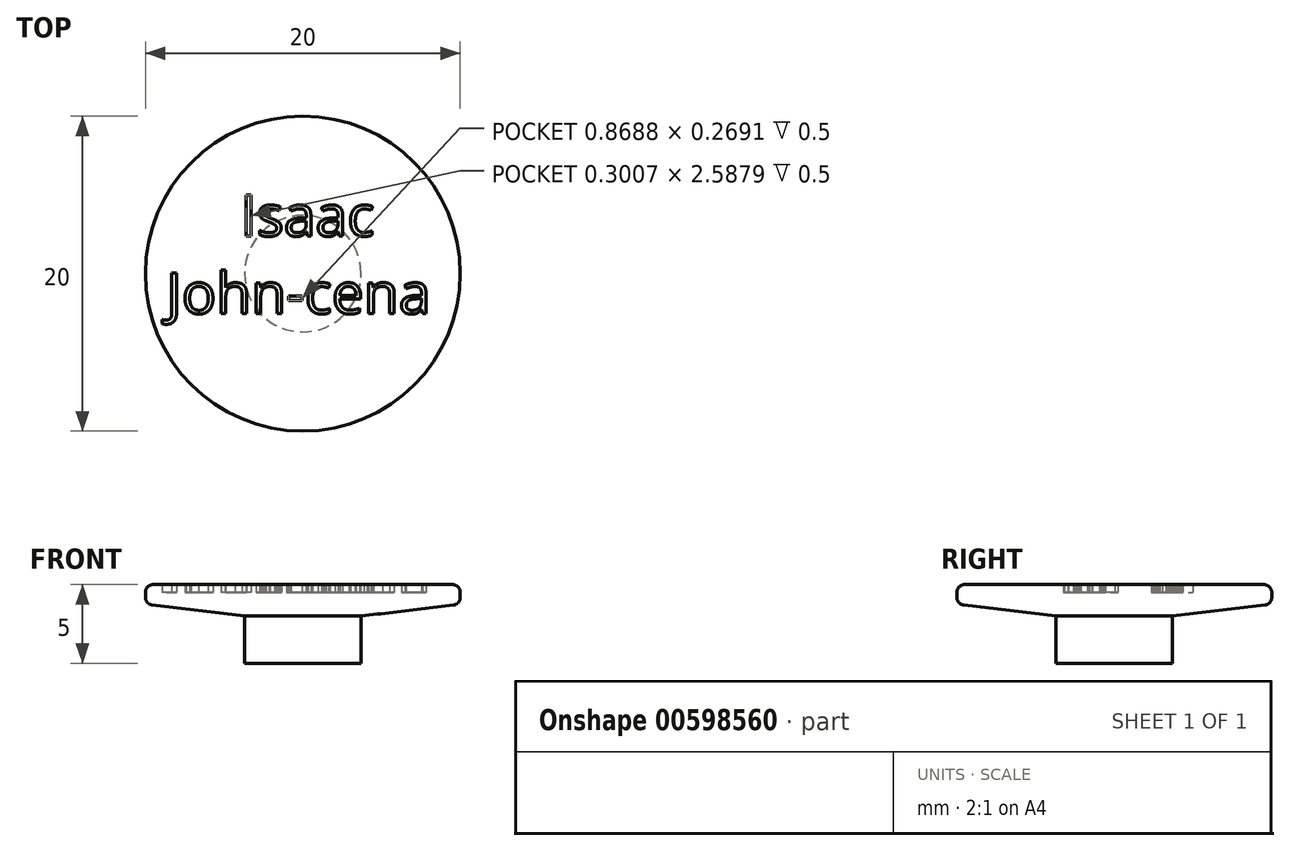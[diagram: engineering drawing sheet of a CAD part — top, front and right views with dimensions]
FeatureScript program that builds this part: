
annotation { "Feature Type Name" : "Feature", "Feature Type Description" : "" }
export const myFeature = defineFeature(function(context is Context, id is Id, definition is map)
    precondition{}
    {
        {
            var Q0;
            Q0=qCreatedBy(makeId("Front.planeOp"),FACE);
            var sketch = newSketch(context, id + "F0", { "sketchPlane" : qUnion([Q0])});
            skLineSegment(sketch, "E0.bottom", {"start": v(0, 0) * mm, "end": v(10, 0) * mm});
            skLineSegment(sketch, "E0.top", {"start": v(0, -1.5) * mm, "end": v(3.7, -1.5) * mm});
            skLineSegment(sketch, "E0.left", {"start": v(0, 0) * mm, "end": v(0, -1.5) * mm});
            skLineSegment(sketch, "E0.right", {"start": v(10, 0) * mm, "end": v(10, -0.75) * mm});
            skLineSegment(sketch, "E1.top", {"start": v(0, -4.5) * mm, "end": v(3.7, -4.5) * mm});
            skLineSegment(sketch, "E1.left", {"start": v(0, -1.5) * mm, "end": v(0, -4.5) * mm});
            skLineSegment(sketch, "E1.right", {"start": v(3.7, -1.5) * mm, "end": v(3.7, -4.5) * mm});
            skLineSegment(sketch, "E2", {"start": v(3.7, -1.5) * mm, "end": v(10, -0.75) * mm});
            skPoint(sketch, "E3.orphan", {"position": v(10, -1.5) * mm});
            skSolve(sketch);
        }
        {
            var Q0;
            Q0 = qSketchRegion(id + "F0", true);
            var Q1;
            Q1=sQuery(id+"F0.wireOp",EDGE,"E1.left");
            revolve(context, id + "F1", {"entities" : qUnion([Q0]), "axis" : qUnion([Q1]), "revolveType" : RevolveType.FULL});
        }
        {
            var Q0;
            Q0=makeQuery(id+"F1.opRevolve","SWEPT_FACE",FACE,{"disambiguationData":[OSD([sQuery(id+"F0.wireOp",EDGE,"E0.bottom")])]});
            var sketch = newSketch(context, id + "F2", { "sketchPlane" : qUnion([Q0])});
            skText(sketch, "E4", { "text": "     Isaac\nJohn-cena", "fontName": "OpenSans-Regular.ttf"});
            skPoint(sketch, "E5", {"position": v(-10, 0) * mm});
            skPoint(sketch, "E6", {"position": v(0, 10) * mm});
            const initialGuessF2  = {"E4": [-0.00866, 0.00239, 1, 0, 0.00261]};
            skSetInitialGuess(sketch, initialGuessF2);
            skSolve(sketch);
        }
        {
            var Q0;
            Q0=makeQuery(id+"F2.imprint","IMPRINT",FACE,{"disambiguationData":[TD([[makeQuery(id+"F2.imprint","IMPRINT",EDGE,{"derivedFrom":sQuery(id+"F2.wireOp",EDGE,"E4.sketch_text.stroke-0")}),1.0]])]});
            var Q1;
            Q1=makeQuery(id+"F2.imprint","IMPRINT",FACE,{"disambiguationData":[TD([[makeQuery(id+"F2.imprint","IMPRINT",EDGE,{"derivedFrom":sQuery(id+"F2.wireOp",EDGE,"E4.sketch_text.stroke-48")}),1.0]])]});
            var Q2;
            Q2=makeQuery(id+"F2.imprint","IMPRINT",FACE,{"disambiguationData":[TD([[makeQuery(id+"F2.imprint","IMPRINT",EDGE,{"derivedFrom":sQuery(id+"F2.wireOp",EDGE,"E4.sketch_text.stroke-75")}),1.0]])]});
            var Q3;
            Q3=makeQuery(id+"F2.imprint","IMPRINT",FACE,{"disambiguationData":[TD([[makeQuery(id+"F2.imprint","IMPRINT",EDGE,{"derivedFrom":sQuery(id+"F2.wireOp",EDGE,"E4.sketch_text.stroke-117")}),1.0]])]});
            var Q4;
            Q4=makeQuery(id+"F2.imprint","IMPRINT",FACE,{"disambiguationData":[TD([[makeQuery(id+"F2.imprint","IMPRINT",EDGE,{"derivedFrom":sQuery(id+"F2.wireOp",EDGE,"E4.sketch_text.stroke-193")}),1.0]])]});
            var Q5;
            Q5=makeQuery(id+"F2.imprint","IMPRINT",FACE,{"disambiguationData":[TD([[makeQuery(id+"F2.imprint","IMPRINT",EDGE,{"derivedFrom":sQuery(id+"F2.wireOp",EDGE,"E4.sketch_text.stroke-234")}),1.0]])]});
            extrude(context, id + "F3", {"entities" : qUnion([Q0, Q1, Q2, Q3, Q4, Q5]), "operationType" : NewBodyOperationType.ADD, "depth" : .5 * mm, "offsetDistance" : 25.4 * mm});
        }
        {
            var Q0;
            Q0=makeQuery(id+"F1.opRevolve","SWEPT_EDGE",EDGE,{"disambiguationData":[OSD([sQuery(id+"F0.wireOp",EDGE,"E0.right"),sQuery(id+"F0.wireOp",EDGE,"E2")])]});
            var Q1;
            Q1=makeQuery(id+"F3.opExtrude","CAP_EDGE",EDGE,{"disambiguationData":[OSD([sQuery(id+"F0.wireOp",EDGE,"E0.bottom"),sQuery(id+"F0.wireOp",EDGE,"E0.right")])],"isStart":false});
            fillet(context, id + "F4", {"entities" : qUnion([Q0, Q1]), "radius" : .5 * mm, "tangentPropagation" : true, "allowEdgeOverflow" : false});
        }
    });
